# Revit family: AS_0530_50_S26_2D
name_source: partatom
category: Mechanical Equipment
revit_build: Autodesk Revit 2018 (Build: 20170223_1515(x64)
units: mm (PartAtom-declared; Revit-internal decimal feet)

## family parameters
Always vertical = Yes
Cut with Voids When Loaded = No
Part Type = Normal
Room Calculation Point = No
Round Connector Dimension = Use Radius
Shared = No
Work Plane-Based = No

## types (1)
- AS0530 S26/2D
    Bottom Plate = Cast Iron EN-GJL-250
    Cable Length (m) = As Per Specification
    Cable Size = Standard = 4G1.5, EX = 7G1.5
    Capacity (m3/hr) = 80 m³
    Description = Robust, reliable submersible pumps from 1 to 3 kW for
pumping clear water, wastewater and sewage from buildings
and sites in domestic and commercial areas.
    Fasteners = Stainless steel 1.4401 (AISI 316)
    Head (m) = 35 mm  [stored 0.114829 ft]
    Impeller = Cast Iron EN-GJL-250
    Manufacturer = Sulzer
    Model = Submersible Wastewater Pump Type ABS AS 0530
    Motor Housing = Cast Iron EN-GJL-250
    Motor Power (kW) = P1=3.43 P2=2.60
    Product Specification Link = https://www.sulzer.com
    Rated Current (A) = 5.64
    Rated Voltage (V) = 400 3~
    Rotor Shaft = Stainless steel 1.4021 (AISI 420)
    Speed (r/min) = 2900
    Volute = Cast Iron EN-GJL-250

note: [stored X ft] marks values corroborated as IEEE doubles in the binary element streams (Revit-internal decimal feet)

## geometry (parser evidence)
native form markers: Sweep x3
no freeform markers — native parametric forms only
